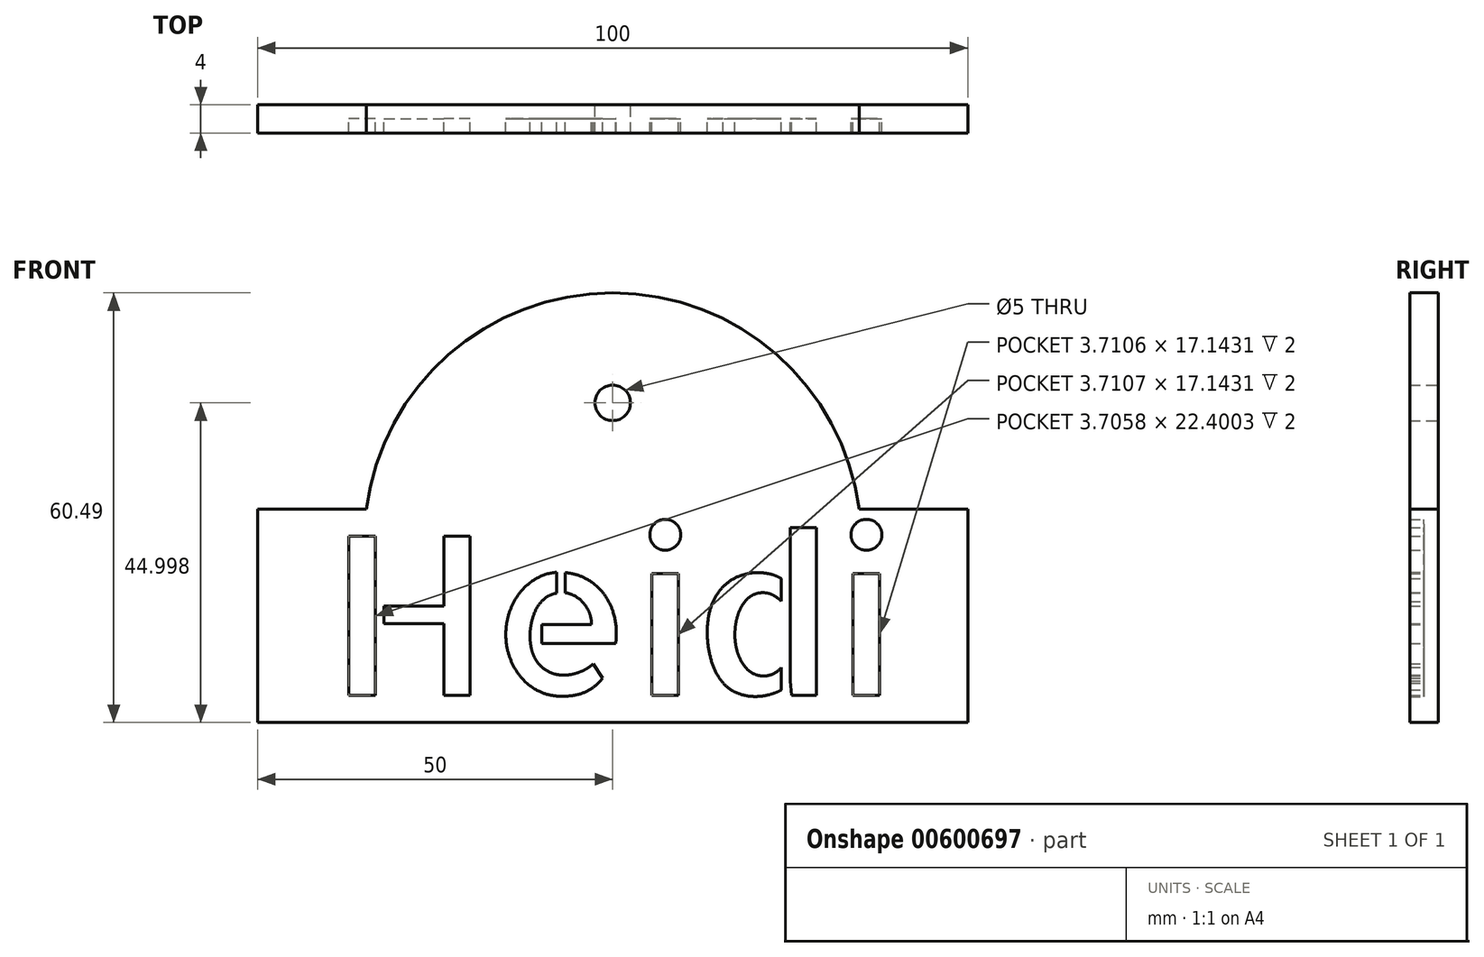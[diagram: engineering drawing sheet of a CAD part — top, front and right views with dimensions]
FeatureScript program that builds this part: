
annotation { "Feature Type Name" : "Feature", "Feature Type Description" : "" }
export const myFeature = defineFeature(function(context is Context, id is Id, definition is map)
    precondition{}
    {
        {
            var Q0;
            Q0=qCreatedBy(makeId("Front.planeOp"),FACE);
            var sketch = newSketch(context, id + "F0", { "sketchPlane" : qUnion([Q0])});
            skLineSegment(sketch, "E0.bottom", {"start": v(-86.2, 30.25) * mm, "end": v(-70.9, 30.25) * mm});
            skLineSegment(sketch, "E0.top", {"start": v(-86.2, 0.25) * mm, "end": v(13.8, 0.25) * mm});
            skLineSegment(sketch, "E0.left", {"start": v(-86.2, 30.25) * mm, "end": v(-86.2, 0.25) * mm});
            skLineSegment(sketch, "E0.right", {"start": v(13.8, 30.25) * mm, "end": v(13.8, 0.25) * mm});
            skArc(sketch, "E1", {"start": v(-1.5, 30.25) * mm, "mid": v(-36.2, 60.74) * mm, "end": v(-70.9, 30.25) * mm});
            skCircle(sketch, "E2", {"center": v(-36.2, 45.25) * mm, "radius": 2.5 * mm});
            skText(sketch, "E3", { "text": "Heidi", "fontName": "AllertaStencil-Regular.ttf"});
            skPoint(sketch, "E4", {"position": v(13.8, 15.25) * mm});
            skPoint(sketch, "E5", {"position": v(-36.2, 0.25) * mm});
            skPoint(sketch, "E6", {"position": v(-36.2, 4.04) * mm});
            skPoint(sketch, "E7", {"position": v(-36.2, 60.74) * mm});
            skPoint(sketch, "E8", {"position": v(3.8, 15.25) * mm});
            skPoint(sketch, "E9", {"position": v(-76.2, 15.25) * mm});
            skLineSegment(sketch, "E10.trimOffspring", {"start": v(-1.5, 30.25) * mm, "end": v(13.8, 30.25) * mm});
            const initialGuessF0  = {"E3": [-0.0762, 0.00404, 1, 0, 0.02241]};
            skSetInitialGuess(sketch, initialGuessF0);
            skSolve(sketch);
        }
        {
            var Q0;
            Q0 = qSketchRegion(id + "F0", true);
            var Q1;
            Q1=makeQuery(id+"F0.imprint","IMPRINT",FACE,{"disambiguationData":[TD([[makeQuery(id+"F0.imprint","IMPRINT",EDGE,{"derivedFrom":sQuery(id+"F0.wireOp",EDGE,"E3.sketch_text.stroke-66")}),-1.0]])]});
            var Q2;
            Q2=makeQuery(id+"F0.imprint","IMPRINT",FACE,{"disambiguationData":[TD([[makeQuery(id+"F0.imprint","IMPRINT",EDGE,{"derivedFrom":sQuery(id+"F0.wireOp",EDGE,"E3.sketch_text.stroke-91")}),-1.0]])]});
            var Q3;
            Q3=makeQuery(id+"F0.imprint","IMPRINT",FACE,{"disambiguationData":[TD([[makeQuery(id+"F0.imprint","IMPRINT",EDGE,{"derivedFrom":sQuery(id+"F0.wireOp",EDGE,"E3.sketch_text.stroke-61")}),-1.0]])]});
            var Q4;
            Q4=makeQuery(id+"F0.imprint","IMPRINT",FACE,{"disambiguationData":[TD([[makeQuery(id+"F0.imprint","IMPRINT",EDGE,{"derivedFrom":sQuery(id+"F0.wireOp",EDGE,"E3.sketch_text.stroke-49")}),-1.0]])]});
            var Q5;
            Q5=makeQuery(id+"F0.imprint","IMPRINT",FACE,{"disambiguationData":[TD([[makeQuery(id+"F0.imprint","IMPRINT",EDGE,{"derivedFrom":sQuery(id+"F0.wireOp",EDGE,"E3.sketch_text.stroke-25")}),-1.0]])]});
            var Q6;
            Q6=makeQuery(id+"F0.imprint","IMPRINT",FACE,{"disambiguationData":[TD([[makeQuery(id+"F0.imprint","IMPRINT",EDGE,{"derivedFrom":sQuery(id+"F0.wireOp",EDGE,"E3.sketch_text.stroke-12")}),-1.0]])]});
            var Q7;
            Q7=makeQuery(id+"F0.imprint","IMPRINT",FACE,{"disambiguationData":[TD([[makeQuery(id+"F0.imprint","IMPRINT",EDGE,{"derivedFrom":sQuery(id+"F0.wireOp",EDGE,"E3.sketch_text.stroke-8")}),-1.0]])]});
            var Q8;
            Q8=makeQuery(id+"F0.imprint","IMPRINT",FACE,{"disambiguationData":[TD([[makeQuery(id+"F0.imprint","IMPRINT",EDGE,{"derivedFrom":sQuery(id+"F0.wireOp",EDGE,"E3.sketch_text.stroke-0")}),-1.0]])]});
            var Q9;
            Q9=makeQuery(id+"F0.imprint","IMPRINT",FACE,{"disambiguationData":[TD([[makeQuery(id+"F0.imprint","IMPRINT",EDGE,{"derivedFrom":sQuery(id+"F0.wireOp",EDGE,"E0.bottom")}),-1.0]])]});
            var Q10;
            Q10=makeQuery(id+"F0.imprint","IMPRINT",FACE,{"disambiguationData":[TD([[makeQuery(id+"F0.imprint","IMPRINT",EDGE,{"derivedFrom":sQuery(id+"F0.wireOp",EDGE,"E3.sketch_text.stroke-95")}),-1.0]])]});
            var Q11;
            Q11=makeQuery(id+"F0.imprint","IMPRINT",FACE,{"disambiguationData":[TD([[makeQuery(id+"F0.imprint","IMPRINT",EDGE,{"derivedFrom":sQuery(id+"F0.wireOp",EDGE,"E3.sketch_text.stroke-53")}),-1.0]])]});
            var Q12;
            {var subQ0=sQuery(id+"F0.wireOp",EDGE,"E3.sketch_text.stroke-101");var subQ1=sQuery(id+"F0.wireOp",EDGE,"E3.sketch_text.stroke-100");var subQ2=makeQuery(id+"F0.imprint","INTERSECT",VERTEX,{"derivedFrom":[subQ1,subQ0]});Q12=makeQuery(id+"F0.imprint","IMPRINT",FACE,{"disambiguationData":[TD([[makeQuery(id+"F0.imprint","IMPRINT",EDGE,{"disambiguationData":[TD([[subQ2,1.0]])],"derivedFrom":subQ1}),-1.0]])]});}
            extrude(context, id + "F1", {"entities" : qUnion([Q0, Q1, Q2, Q3, Q4, Q5, Q6, Q7, Q8, Q9, Q10, Q11, Q12]), "depth" : 2 * mm, "offsetDistance" : 25 * mm});
        }
        {
            var Q0;
            Q0=makeQuery(id+"F0.imprint","IMPRINT",FACE,{"disambiguationData":[TD([[makeQuery(id+"F0.imprint","IMPRINT",EDGE,{"derivedFrom":sQuery(id+"F0.wireOp",EDGE,"E0.bottom")}),-1.0]])]});
            extrude(context, id + "F2", {"entities" : qUnion([Q0]), "operationType" : NewBodyOperationType.ADD, "depth" : 4 * mm, "offsetDistance" : 25 * mm});
        }
    });
